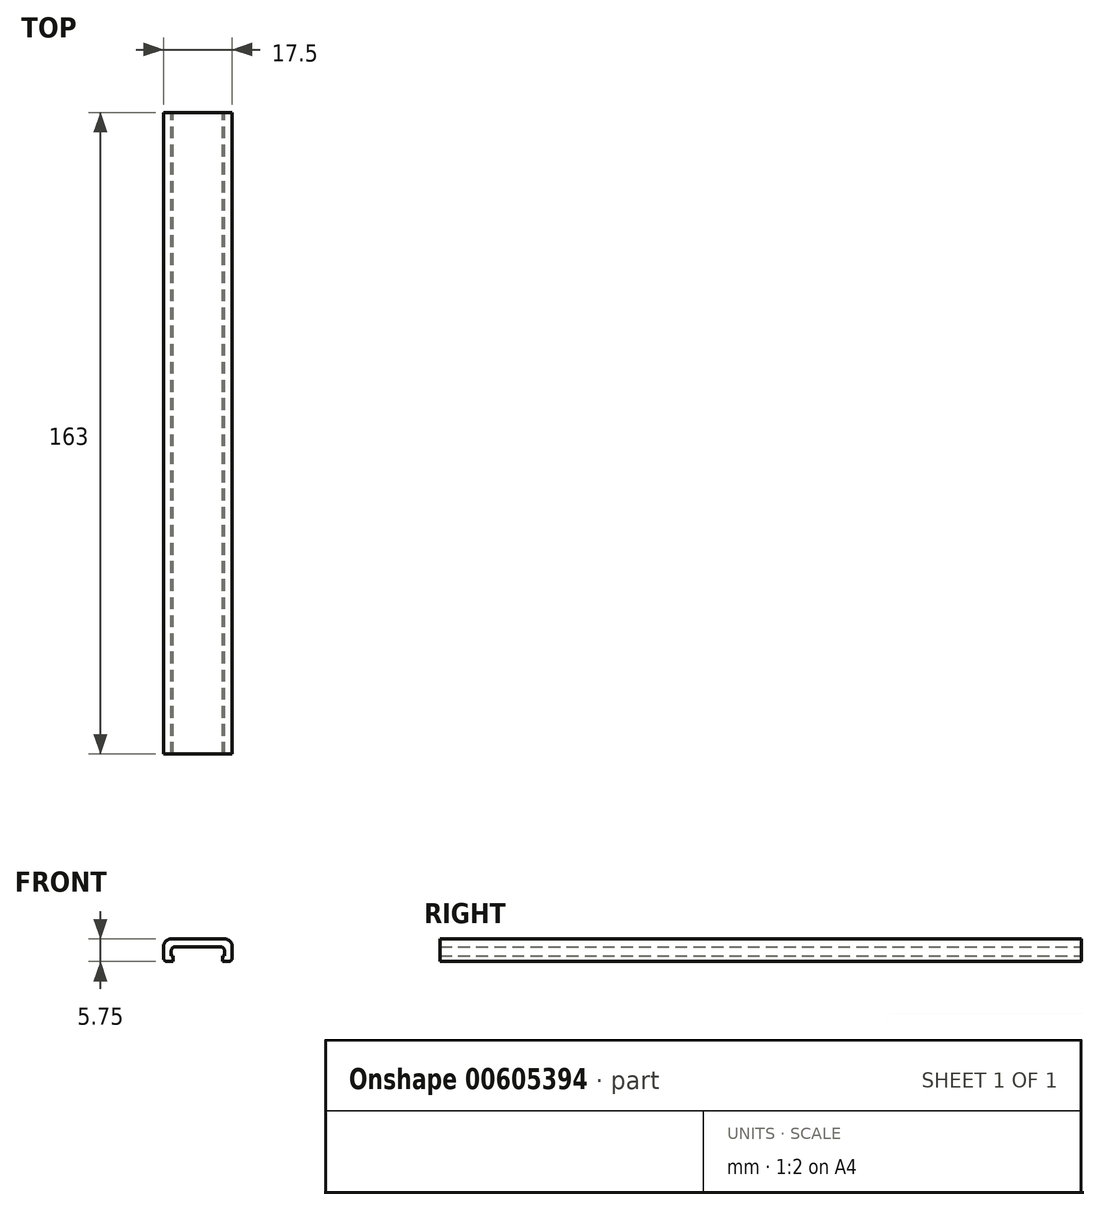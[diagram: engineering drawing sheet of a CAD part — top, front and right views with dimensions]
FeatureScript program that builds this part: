
annotation { "Feature Type Name" : "Feature", "Feature Type Description" : "" }
export const myFeature = defineFeature(function(context is Context, id is Id, definition is map)
    precondition{}
    {
        {
            var Q0;
            Q0=qCreatedBy(makeId("Front.planeOp"),FACE);
            var sketch = newSketch(context, id + "F0", { "sketchPlane" : qUnion([Q0])});
            skLineSegment(sketch, "E0", {"start": v(0, 0) * mm, "end": v(8.75, 0) * mm});
            skLineSegment(sketch, "E1", {"start": v(8.75, 0) * mm, "end": v(8.75, -5.75) * mm});
            skLineSegment(sketch, "E2", {"start": v(8.75, -5.75) * mm, "end": v(6.25, -5.75) * mm});
            skLineSegment(sketch, "E3", {"start": v(6.25, -5.75) * mm, "end": v(6.25, -4.25) * mm});
            skLineSegment(sketch, "E4", {"start": v(6.25, -4.25) * mm, "end": v(6.75, -4.25) * mm});
            skLineSegment(sketch, "E5", {"start": v(6.75, -4.25) * mm, "end": v(6.75, -2) * mm});
            skLineSegment(sketch, "E6", {"start": v(6.75, -2) * mm, "end": v(0, -2) * mm});
            skLineSegment(sketch, "E7", {"start": v(0, -2) * mm, "end": v(0, 0) * mm});
            skSolve(sketch);
        }
        {
            var Q0;
            Q0=makeQuery(id+"F0.imprint","IMPRINT",FACE,{"disambiguationData":[TD([[makeQuery(id+"F0.imprint","IMPRINT",EDGE,{"derivedFrom":sQuery(id+"F0.wireOp",EDGE,"E0")}),-1.0]])]});
            extrude(context, id + "F1", {"entities" : qUnion([Q0]), "depth" : 163 * mm, "offsetDistance" : 25 * mm});
        }
        {
            var Q0;
            Q0=makeQuery(id+"F1.opExtrude","SWEPT_EDGE",EDGE,{"disambiguationData":[OSD([sQuery(id+"F0.wireOp",EDGE,"E0"),sQuery(id+"F0.wireOp",EDGE,"E1")])]});
            fillet(context, id + "F2", {"entities" : qUnion([Q0]), "radius" : 2 * mm, "tangentPropagation" : true, "allowEdgeOverflow" : false});
        }
        {
            var Q0;
            Q0=makeQuery(id+"F1.opExtrude","SWEPT_EDGE",EDGE,{"disambiguationData":[OSD([sQuery(id+"F0.wireOp",EDGE,"E5"),sQuery(id+"F0.wireOp",EDGE,"E6")])]});
            fillet(context, id + "F3", {"entities" : qUnion([Q0]), "radius" : 1 * mm, "tangentPropagation" : true, "allowEdgeOverflow" : false});
        }
        {
            var Q0;
            Q0=makeQuery(id+"F1.opExtrude","SWEPT_EDGE",EDGE,{"disambiguationData":[OSD([sQuery(id+"F0.wireOp",EDGE,"E1"),sQuery(id+"F0.wireOp",EDGE,"E2")])]});
            fillet(context, id + "F4", {"entities" : qUnion([Q0]), "radius" : 1 * mm, "tangentPropagation" : true, "allowEdgeOverflow" : false});
        }
        {
            var Q0;
            Q0=makeQuery(id+"F1.opExtrude","SWEPT_BODY",BODY,{"disambiguationData":[OSD([sQuery(id+"F0.wireOp",EDGE,"E0"),sQuery(id+"F0.wireOp",EDGE,"E1"),sQuery(id+"F0.wireOp",EDGE,"E2"),sQuery(id+"F0.wireOp",EDGE,"E3"),sQuery(id+"F0.wireOp",EDGE,"E4"),sQuery(id+"F0.wireOp",EDGE,"E5"),sQuery(id+"F0.wireOp",EDGE,"E6"),sQuery(id+"F0.wireOp",EDGE,"E7")])]});
            var Q1;
            Q1=qCreatedBy(makeId("Right.planeOp"),FACE);
            mirror(context, id + "F5", {"operationType" : NewBodyOperationType.ADD, "entities" : qUnion([Q0]), "mirrorPlane" : qUnion([Q1])});
        }
    });
